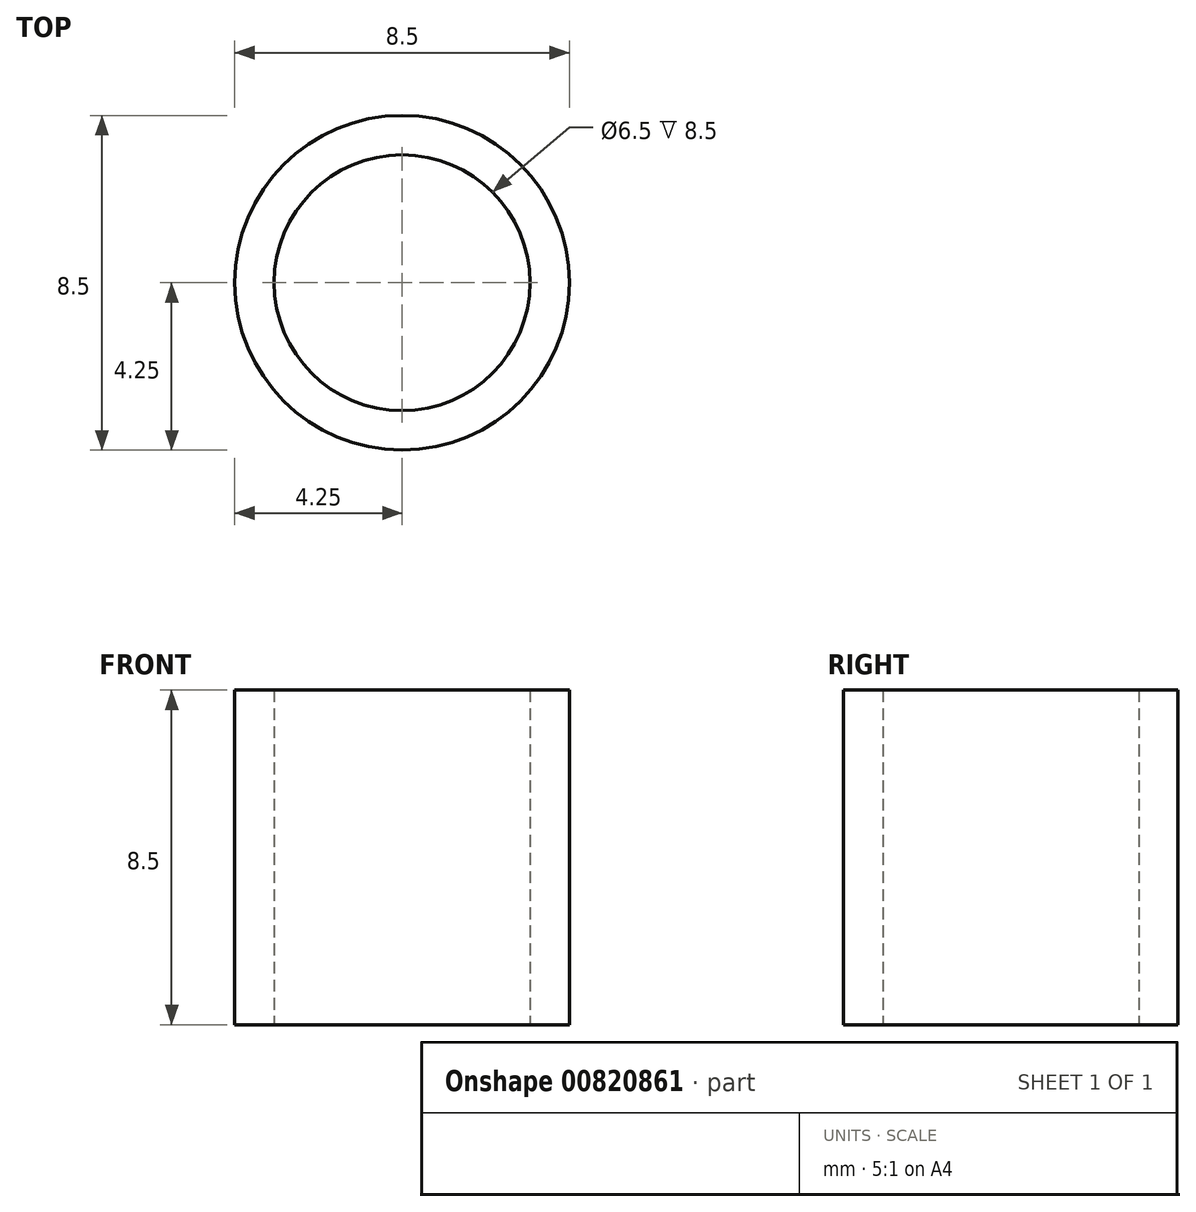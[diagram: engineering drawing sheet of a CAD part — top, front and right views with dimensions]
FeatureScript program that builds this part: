
annotation { "Feature Type Name" : "Feature", "Feature Type Description" : "" }
export const myFeature = defineFeature(function(context is Context, id is Id, definition is map)
    precondition{}
    {
        {
            var Q0;
            Q0=qCreatedBy(makeId("Top.planeOp"),FACE);
            var sketch = newSketch(context, id + "F0", { "sketchPlane" : qUnion([Q0])});
            skCircle(sketch, "E0", {"center": v(0, 0) * mm, "radius": 3.25 * mm});
            skCircle(sketch, "E1", {"center": v(0, 0) * mm, "radius": 4.25 * mm});
            skSolve(sketch);
        }
        {
            var Q0;
            Q0=makeQuery(id+"F0.imprint","IMPRINT",FACE,{"disambiguationData":[TD([[makeQuery(id+"F0.imprint","IMPRINT",EDGE,{"derivedFrom":sQuery(id+"F0.wireOp",EDGE,"E0")}),-1.0]])]});
            extrude(context, id + "F1", {"entities" : qUnion([Q0]), "depth" : 8.5 * mm, "offsetDistance" : 25 * mm});
        }
    });
